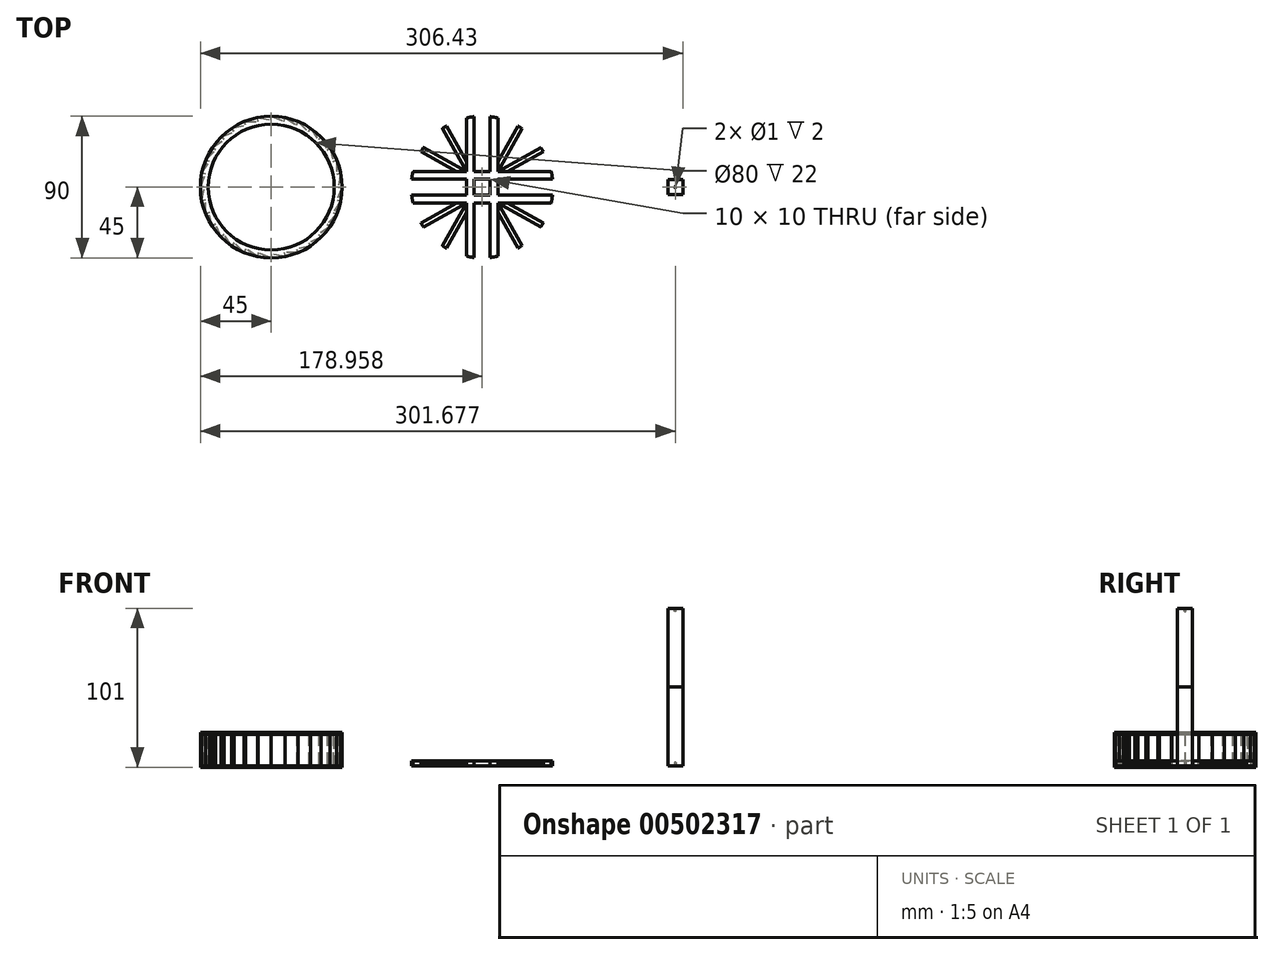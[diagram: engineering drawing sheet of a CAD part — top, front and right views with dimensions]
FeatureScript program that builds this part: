
annotation { "Feature Type Name" : "Feature", "Feature Type Description" : "" }
export const myFeature = defineFeature(function(context is Context, id is Id, definition is map)
    precondition{}
    {
        {
            var Q0;
            Q0=qCreatedBy(makeId("Top.planeOp"),FACE);
            var sketch = newSketch(context, id + "F0", { "sketchPlane" : qUnion([Q0])});
            skCircle(sketch, "E0", {"center": v(0, 0) * mm, "radius": 4.5 * mm});
            skCircle(sketch, "E1", {"center": v(0, 0) * mm, "radius": 4 * mm});
            skLineSegment(sketch, "E2", {"start": v(0, 0) * mm, "end": v(0, 4.5) * mm, "construction": true});
            skLineSegment(sketch, "E3.1.0", {"start": v(0, 0) * mm, "end": v(-0.88, 4.41) * mm, "construction": true});
            skLineSegment(sketch, "E3.2.0", {"start": v(0, 0) * mm, "end": v(-1.72, 4.16) * mm, "construction": true});
            skLineSegment(sketch, "E3.3.0", {"start": v(0, 0) * mm, "end": v(-2.5, 3.74) * mm, "construction": true});
            skLineSegment(sketch, "E3.4.0", {"start": v(0, 0) * mm, "end": v(-3.18, 3.18) * mm, "construction": true});
            skLineSegment(sketch, "E3.5.0", {"start": v(0, 0) * mm, "end": v(-3.74, 2.5) * mm, "construction": true});
            skLineSegment(sketch, "E3.6.0", {"start": v(0, 0) * mm, "end": v(-4.16, 1.72) * mm, "construction": true});
            skLineSegment(sketch, "E3.7.0", {"start": v(0, 0) * mm, "end": v(-4.41, 0.88) * mm, "construction": true});
            skLineSegment(sketch, "E3.8.0", {"start": v(0, 0) * mm, "end": v(-4.5, 0) * mm, "construction": true});
            skLineSegment(sketch, "E3.9.0", {"start": v(0, 0) * mm, "end": v(-4.41, -0.88) * mm, "construction": true});
            skLineSegment(sketch, "E3.10.0", {"start": v(0, 0) * mm, "end": v(-4.16, -1.72) * mm, "construction": true});
            skLineSegment(sketch, "E3.11.0", {"start": v(0, 0) * mm, "end": v(-3.74, -2.5) * mm, "construction": true});
            skLineSegment(sketch, "E3.12.0", {"start": v(0, 0) * mm, "end": v(-3.18, -3.18) * mm, "construction": true});
            skLineSegment(sketch, "E3.13.0", {"start": v(0, 0) * mm, "end": v(-2.5, -3.74) * mm, "construction": true});
            skLineSegment(sketch, "E3.14.0", {"start": v(0, 0) * mm, "end": v(-1.72, -4.16) * mm, "construction": true});
            skLineSegment(sketch, "E3.15.0", {"start": v(0, 0) * mm, "end": v(-0.88, -4.41) * mm, "construction": true});
            skLineSegment(sketch, "E3.16.0", {"start": v(0, 0) * mm, "end": v(0, -4.5) * mm, "construction": true});
            skLineSegment(sketch, "E3.17.0", {"start": v(0, 0) * mm, "end": v(0.88, -4.41) * mm, "construction": true});
            skLineSegment(sketch, "E3.18.0", {"start": v(0, 0) * mm, "end": v(1.72, -4.16) * mm, "construction": true});
            skLineSegment(sketch, "E3.19.0", {"start": v(0, 0) * mm, "end": v(2.5, -3.74) * mm, "construction": true});
            skLineSegment(sketch, "E3.20.0", {"start": v(0, 0) * mm, "end": v(3.18, -3.18) * mm, "construction": true});
            skLineSegment(sketch, "E3.21.0", {"start": v(0, 0) * mm, "end": v(3.74, -2.5) * mm, "construction": true});
            skLineSegment(sketch, "E3.22.0", {"start": v(0, 0) * mm, "end": v(4.16, -1.72) * mm, "construction": true});
            skLineSegment(sketch, "E3.23.0", {"start": v(0, 0) * mm, "end": v(4.41, -0.88) * mm, "construction": true});
            skLineSegment(sketch, "E3.24.0", {"start": v(0, 0) * mm, "end": v(4.5, 0) * mm, "construction": true});
            skLineSegment(sketch, "E3.25.0", {"start": v(0, 0) * mm, "end": v(4.41, 0.88) * mm, "construction": true});
            skLineSegment(sketch, "E3.26.0", {"start": v(0, 0) * mm, "end": v(4.16, 1.72) * mm, "construction": true});
            skLineSegment(sketch, "E3.27.0", {"start": v(0, 0) * mm, "end": v(3.74, 2.5) * mm, "construction": true});
            skLineSegment(sketch, "E3.28.0", {"start": v(0, 0) * mm, "end": v(3.18, 3.18) * mm, "construction": true});
            skLineSegment(sketch, "E3.29.0", {"start": v(0, 0) * mm, "end": v(2.5, 3.74) * mm, "construction": true});
            skLineSegment(sketch, "E3.30.0", {"start": v(0, 0) * mm, "end": v(1.72, 4.16) * mm, "construction": true});
            skLineSegment(sketch, "E3.31.0", {"start": v(0, 0) * mm, "end": v(0.88, 4.41) * mm, "construction": true});
            skCircle(sketch, "E4", {"center": v(0, 0) * mm, "radius": 4.25 * mm, "construction": true});
            skLineSegment(sketch, "E5", {"start": v(0, 4.25) * mm, "end": v(0, 4.5) * mm});
            skLineSegment(sketch, "E6", {"start": v(0, 4.5) * mm, "end": v(0.83, 4.17) * mm});
            skLineSegment(sketch, "E7.1.0", {"start": v(-0.88, 4.41) * mm, "end": v(0, 4.25) * mm});
            skLineSegment(sketch, "E7.1.1", {"start": v(-0.83, 4.17) * mm, "end": v(-0.88, 4.41) * mm});
            skLineSegment(sketch, "E7.2.0", {"start": v(-1.72, 4.16) * mm, "end": v(-0.83, 4.17) * mm});
            skLineSegment(sketch, "E7.2.1", {"start": v(-1.63, 3.93) * mm, "end": v(-1.72, 4.16) * mm});
            skLineSegment(sketch, "E7.3.0", {"start": v(-2.5, 3.74) * mm, "end": v(-1.63, 3.93) * mm});
            skLineSegment(sketch, "E7.3.1", {"start": v(-2.36, 3.53) * mm, "end": v(-2.5, 3.74) * mm});
            skLineSegment(sketch, "E7.4.0", {"start": v(-3.18, 3.18) * mm, "end": v(-2.36, 3.53) * mm});
            skLineSegment(sketch, "E7.4.1", {"start": v(-3, 3) * mm, "end": v(-3.18, 3.18) * mm});
            skLineSegment(sketch, "E7.5.0", {"start": v(-3.74, 2.5) * mm, "end": v(-3, 3) * mm});
            skLineSegment(sketch, "E7.5.1", {"start": v(-3.53, 2.36) * mm, "end": v(-3.74, 2.5) * mm});
            skLineSegment(sketch, "E7.6.0", {"start": v(-4.16, 1.72) * mm, "end": v(-3.53, 2.36) * mm});
            skLineSegment(sketch, "E7.6.1", {"start": v(-3.93, 1.63) * mm, "end": v(-4.16, 1.72) * mm});
            skLineSegment(sketch, "E7.7.0", {"start": v(-4.41, 0.88) * mm, "end": v(-3.93, 1.63) * mm});
            skLineSegment(sketch, "E7.7.1", {"start": v(-4.17, 0.83) * mm, "end": v(-4.41, 0.88) * mm});
            skLineSegment(sketch, "E7.8.0", {"start": v(-4.5, 0) * mm, "end": v(-4.17, 0.83) * mm});
            skLineSegment(sketch, "E7.8.1", {"start": v(-4.25, 0) * mm, "end": v(-4.5, 0) * mm});
            skLineSegment(sketch, "E7.9.0", {"start": v(-4.41, -0.88) * mm, "end": v(-4.25, 0) * mm});
            skLineSegment(sketch, "E7.9.1", {"start": v(-4.17, -0.83) * mm, "end": v(-4.41, -0.88) * mm});
            skLineSegment(sketch, "E7.10.0", {"start": v(-4.16, -1.72) * mm, "end": v(-4.17, -0.83) * mm});
            skLineSegment(sketch, "E7.10.1", {"start": v(-3.93, -1.63) * mm, "end": v(-4.16, -1.72) * mm});
            skLineSegment(sketch, "E7.11.0", {"start": v(-3.74, -2.5) * mm, "end": v(-3.93, -1.63) * mm});
            skLineSegment(sketch, "E7.11.1", {"start": v(-3.53, -2.36) * mm, "end": v(-3.74, -2.5) * mm});
            skLineSegment(sketch, "E7.12.0", {"start": v(-3.18, -3.18) * mm, "end": v(-3.53, -2.36) * mm});
            skLineSegment(sketch, "E7.12.1", {"start": v(-3, -3) * mm, "end": v(-3.18, -3.18) * mm});
            skLineSegment(sketch, "E7.13.0", {"start": v(-2.5, -3.74) * mm, "end": v(-3, -3) * mm});
            skLineSegment(sketch, "E7.13.1", {"start": v(-2.36, -3.53) * mm, "end": v(-2.5, -3.74) * mm});
            skLineSegment(sketch, "E7.14.0", {"start": v(-1.72, -4.16) * mm, "end": v(-2.36, -3.53) * mm});
            skLineSegment(sketch, "E7.14.1", {"start": v(-1.63, -3.93) * mm, "end": v(-1.72, -4.16) * mm});
            skLineSegment(sketch, "E7.15.0", {"start": v(-0.88, -4.41) * mm, "end": v(-1.63, -3.93) * mm});
            skLineSegment(sketch, "E7.15.1", {"start": v(-0.83, -4.17) * mm, "end": v(-0.88, -4.41) * mm});
            skLineSegment(sketch, "E7.16.0", {"start": v(0, -4.5) * mm, "end": v(-0.83, -4.17) * mm});
            skLineSegment(sketch, "E7.16.1", {"start": v(0, -4.25) * mm, "end": v(0, -4.5) * mm});
            skLineSegment(sketch, "E7.17.0", {"start": v(0.88, -4.41) * mm, "end": v(0, -4.25) * mm});
            skLineSegment(sketch, "E7.17.1", {"start": v(0.83, -4.17) * mm, "end": v(0.88, -4.41) * mm});
            skLineSegment(sketch, "E7.18.0", {"start": v(1.72, -4.16) * mm, "end": v(0.83, -4.17) * mm});
            skLineSegment(sketch, "E7.18.1", {"start": v(1.63, -3.93) * mm, "end": v(1.72, -4.16) * mm});
            skLineSegment(sketch, "E7.19.0", {"start": v(2.5, -3.74) * mm, "end": v(1.63, -3.93) * mm});
            skLineSegment(sketch, "E7.19.1", {"start": v(2.36, -3.53) * mm, "end": v(2.5, -3.74) * mm});
            skLineSegment(sketch, "E7.20.0", {"start": v(3.18, -3.18) * mm, "end": v(2.36, -3.53) * mm});
            skLineSegment(sketch, "E7.20.1", {"start": v(3, -3) * mm, "end": v(3.18, -3.18) * mm});
            skLineSegment(sketch, "E7.21.0", {"start": v(3.74, -2.5) * mm, "end": v(3, -3) * mm});
            skLineSegment(sketch, "E7.21.1", {"start": v(3.53, -2.36) * mm, "end": v(3.74, -2.5) * mm});
            skLineSegment(sketch, "E7.22.0", {"start": v(4.16, -1.72) * mm, "end": v(3.53, -2.36) * mm});
            skLineSegment(sketch, "E7.22.1", {"start": v(3.93, -1.63) * mm, "end": v(4.16, -1.72) * mm});
            skLineSegment(sketch, "E7.23.0", {"start": v(4.41, -0.88) * mm, "end": v(3.93, -1.63) * mm});
            skLineSegment(sketch, "E7.23.1", {"start": v(4.17, -0.83) * mm, "end": v(4.41, -0.88) * mm});
            skLineSegment(sketch, "E7.24.0", {"start": v(4.5, 0) * mm, "end": v(4.17, -0.83) * mm});
            skLineSegment(sketch, "E7.24.1", {"start": v(4.25, 0) * mm, "end": v(4.5, 0) * mm});
            skLineSegment(sketch, "E7.25.0", {"start": v(4.41, 0.88) * mm, "end": v(4.25, 0) * mm});
            skLineSegment(sketch, "E7.25.1", {"start": v(4.17, 0.83) * mm, "end": v(4.41, 0.88) * mm});
            skLineSegment(sketch, "E7.26.0", {"start": v(4.16, 1.72) * mm, "end": v(4.17, 0.83) * mm});
            skLineSegment(sketch, "E7.26.1", {"start": v(3.93, 1.63) * mm, "end": v(4.16, 1.72) * mm});
            skLineSegment(sketch, "E7.27.0", {"start": v(3.74, 2.5) * mm, "end": v(3.93, 1.63) * mm});
            skLineSegment(sketch, "E7.27.1", {"start": v(3.53, 2.36) * mm, "end": v(3.74, 2.5) * mm});
            skLineSegment(sketch, "E7.28.0", {"start": v(3.18, 3.18) * mm, "end": v(3.53, 2.36) * mm});
            skLineSegment(sketch, "E7.28.1", {"start": v(3, 3) * mm, "end": v(3.18, 3.18) * mm});
            skLineSegment(sketch, "E7.29.0", {"start": v(2.5, 3.74) * mm, "end": v(3, 3) * mm});
            skLineSegment(sketch, "E7.29.1", {"start": v(2.36, 3.53) * mm, "end": v(2.5, 3.74) * mm});
            skLineSegment(sketch, "E7.30.0", {"start": v(1.72, 4.16) * mm, "end": v(2.36, 3.53) * mm});
            skLineSegment(sketch, "E7.30.1", {"start": v(1.63, 3.93) * mm, "end": v(1.72, 4.16) * mm});
            skLineSegment(sketch, "E7.31.0", {"start": v(0.88, 4.41) * mm, "end": v(1.63, 3.93) * mm});
            skLineSegment(sketch, "E7.31.1", {"start": v(0.83, 4.17) * mm, "end": v(0.88, 4.41) * mm});
            skSolve(sketch);
        }
        {
            var Q0;
            Q0=makeQuery(id+"F0.imprint","IMPRINT",FACE,{"disambiguationData":[TD([[makeQuery(id+"F0.imprint","IMPRINT",EDGE,{"derivedFrom":sQuery(id+"F0.wireOp",EDGE,"E1")}),-1.0]])]});
            extrude(context, id + "F1", {"entities" : qUnion([Q0]), "depth" : 1 * mm});
        }
        {
            var Q0;
            {var subQ0=sQuery(id+"F0.wireOp",EDGE,"E7.29.1");Q0=makeQuery(id+"F0.imprint","IMPRINT",FACE,{"disambiguationData":[TD([[makeQuery(id+"F0.imprint","IMPRINT",EDGE,{"derivedFrom":subQ0}),1.0]])]});}
            var Q1;
            {var subQ0=sQuery(id+"F0.wireOp",EDGE,"E7.6.1");Q1=makeQuery(id+"F0.imprint","IMPRINT",FACE,{"disambiguationData":[TD([[makeQuery(id+"F0.imprint","IMPRINT",EDGE,{"derivedFrom":subQ0}),1.0]])]});}
            var Q2;
            {var subQ0=sQuery(id+"F0.wireOp",EDGE,"E7.18.1");Q2=makeQuery(id+"F0.imprint","IMPRINT",FACE,{"disambiguationData":[TD([[makeQuery(id+"F0.imprint","IMPRINT",EDGE,{"derivedFrom":subQ0}),1.0]])]});}
            var Q3;
            {var subQ0=sQuery(id+"F0.wireOp",EDGE,"E7.28.1");Q3=makeQuery(id+"F0.imprint","IMPRINT",FACE,{"disambiguationData":[TD([[makeQuery(id+"F0.imprint","IMPRINT",EDGE,{"derivedFrom":subQ0}),1.0]])]});}
            var Q4;
            {var subQ0=sQuery(id+"F0.wireOp",EDGE,"E7.8.1");Q4=makeQuery(id+"F0.imprint","IMPRINT",FACE,{"disambiguationData":[TD([[makeQuery(id+"F0.imprint","IMPRINT",EDGE,{"derivedFrom":subQ0}),1.0]])]});}
            var Q5;
            {var subQ0=sQuery(id+"F0.wireOp",EDGE,"E7.26.1");Q5=makeQuery(id+"F0.imprint","IMPRINT",FACE,{"disambiguationData":[TD([[makeQuery(id+"F0.imprint","IMPRINT",EDGE,{"derivedFrom":subQ0}),1.0]])]});}
            var Q6;
            {var subQ0=sQuery(id+"F0.wireOp",EDGE,"E7.7.1");Q6=makeQuery(id+"F0.imprint","IMPRINT",FACE,{"disambiguationData":[TD([[makeQuery(id+"F0.imprint","IMPRINT",EDGE,{"derivedFrom":subQ0}),1.0]])]});}
            var Q7;
            {var subQ0=sQuery(id+"F0.wireOp",EDGE,"E7.10.1");Q7=makeQuery(id+"F0.imprint","IMPRINT",FACE,{"disambiguationData":[TD([[makeQuery(id+"F0.imprint","IMPRINT",EDGE,{"derivedFrom":subQ0}),1.0]])]});}
            var Q8;
            {var subQ0=sQuery(id+"F0.wireOp",EDGE,"E7.24.1");Q8=makeQuery(id+"F0.imprint","IMPRINT",FACE,{"disambiguationData":[TD([[makeQuery(id+"F0.imprint","IMPRINT",EDGE,{"derivedFrom":subQ0}),1.0]])]});}
            var Q9;
            {var subQ0=sQuery(id+"F0.wireOp",EDGE,"E7.23.1");Q9=makeQuery(id+"F0.imprint","IMPRINT",FACE,{"disambiguationData":[TD([[makeQuery(id+"F0.imprint","IMPRINT",EDGE,{"derivedFrom":subQ0}),1.0]])]});}
            var Q10;
            {var subQ0=sQuery(id+"F0.wireOp",EDGE,"E7.4.1");Q10=makeQuery(id+"F0.imprint","IMPRINT",FACE,{"disambiguationData":[TD([[makeQuery(id+"F0.imprint","IMPRINT",EDGE,{"derivedFrom":subQ0}),1.0]])]});}
            var Q11;
            {var subQ0=sQuery(id+"F0.wireOp",EDGE,"E7.20.1");Q11=makeQuery(id+"F0.imprint","IMPRINT",FACE,{"disambiguationData":[TD([[makeQuery(id+"F0.imprint","IMPRINT",EDGE,{"derivedFrom":subQ0}),1.0]])]});}
            var Q12;
            {var subQ0=sQuery(id+"F0.wireOp",EDGE,"E7.3.1");Q12=makeQuery(id+"F0.imprint","IMPRINT",FACE,{"disambiguationData":[TD([[makeQuery(id+"F0.imprint","IMPRINT",EDGE,{"derivedFrom":subQ0}),1.0]])]});}
            var Q13;
            {var subQ0=sQuery(id+"F0.wireOp",EDGE,"E7.13.1");Q13=makeQuery(id+"F0.imprint","IMPRINT",FACE,{"disambiguationData":[TD([[makeQuery(id+"F0.imprint","IMPRINT",EDGE,{"derivedFrom":subQ0}),1.0]])]});}
            var Q14;
            {var subQ0=sQuery(id+"F0.wireOp",EDGE,"E7.14.1");Q14=makeQuery(id+"F0.imprint","IMPRINT",FACE,{"disambiguationData":[TD([[makeQuery(id+"F0.imprint","IMPRINT",EDGE,{"derivedFrom":subQ0}),1.0]])]});}
            var Q15;
            {var subQ0=sQuery(id+"F0.wireOp",EDGE,"E7.17.1");Q15=makeQuery(id+"F0.imprint","IMPRINT",FACE,{"disambiguationData":[TD([[makeQuery(id+"F0.imprint","IMPRINT",EDGE,{"derivedFrom":subQ0}),1.0]])]});}
            var Q16;
            {var subQ0=sQuery(id+"F0.wireOp",EDGE,"E7.11.1");Q16=makeQuery(id+"F0.imprint","IMPRINT",FACE,{"disambiguationData":[TD([[makeQuery(id+"F0.imprint","IMPRINT",EDGE,{"derivedFrom":subQ0}),1.0]])]});}
            var Q17;
            {var subQ0=sQuery(id+"F0.wireOp",EDGE,"E7.19.1");Q17=makeQuery(id+"F0.imprint","IMPRINT",FACE,{"disambiguationData":[TD([[makeQuery(id+"F0.imprint","IMPRINT",EDGE,{"derivedFrom":subQ0}),1.0]])]});}
            var Q18;
            {var subQ0=sQuery(id+"F0.wireOp",EDGE,"E7.1.1");Q18=makeQuery(id+"F0.imprint","IMPRINT",FACE,{"disambiguationData":[TD([[makeQuery(id+"F0.imprint","IMPRINT",EDGE,{"derivedFrom":subQ0}),1.0]])]});}
            var Q19;
            Q19=makeQuery(id+"F0.imprint","IMPRINT",FACE,{"disambiguationData":[TD([[makeQuery(id+"F0.imprint","IMPRINT",EDGE,{"derivedFrom":sQuery(id+"F0.wireOp",EDGE,"E1")}),-1.0]])]});
            var Q20;
            {var subQ0=sQuery(id+"F0.wireOp",EDGE,"E7.5.1");Q20=makeQuery(id+"F0.imprint","IMPRINT",FACE,{"disambiguationData":[TD([[makeQuery(id+"F0.imprint","IMPRINT",EDGE,{"derivedFrom":subQ0}),1.0]])]});}
            var Q21;
            {var subQ0=sQuery(id+"F0.wireOp",EDGE,"E7.16.1");Q21=makeQuery(id+"F0.imprint","IMPRINT",FACE,{"disambiguationData":[TD([[makeQuery(id+"F0.imprint","IMPRINT",EDGE,{"derivedFrom":subQ0}),1.0]])]});}
            var Q22;
            {var subQ0=sQuery(id+"F0.wireOp",EDGE,"E7.25.1");Q22=makeQuery(id+"F0.imprint","IMPRINT",FACE,{"disambiguationData":[TD([[makeQuery(id+"F0.imprint","IMPRINT",EDGE,{"derivedFrom":subQ0}),1.0]])]});}
            var Q23;
            {var subQ0=sQuery(id+"F0.wireOp",EDGE,"E7.12.1");Q23=makeQuery(id+"F0.imprint","IMPRINT",FACE,{"disambiguationData":[TD([[makeQuery(id+"F0.imprint","IMPRINT",EDGE,{"derivedFrom":subQ0}),1.0]])]});}
            var Q24;
            {var subQ0=sQuery(id+"F0.wireOp",EDGE,"E7.2.1");Q24=makeQuery(id+"F0.imprint","IMPRINT",FACE,{"disambiguationData":[TD([[makeQuery(id+"F0.imprint","IMPRINT",EDGE,{"derivedFrom":subQ0}),1.0]])]});}
            var Q25;
            {var subQ0=sQuery(id+"F0.wireOp",EDGE,"E7.9.1");Q25=makeQuery(id+"F0.imprint","IMPRINT",FACE,{"disambiguationData":[TD([[makeQuery(id+"F0.imprint","IMPRINT",EDGE,{"derivedFrom":subQ0}),1.0]])]});}
            var Q26;
            {var subQ0=sQuery(id+"F0.wireOp",EDGE,"E7.30.1");Q26=makeQuery(id+"F0.imprint","IMPRINT",FACE,{"disambiguationData":[TD([[makeQuery(id+"F0.imprint","IMPRINT",EDGE,{"derivedFrom":subQ0}),1.0]])]});}
            var Q27;
            {var subQ0=sQuery(id+"F0.wireOp",EDGE,"E7.27.1");Q27=makeQuery(id+"F0.imprint","IMPRINT",FACE,{"disambiguationData":[TD([[makeQuery(id+"F0.imprint","IMPRINT",EDGE,{"derivedFrom":subQ0}),1.0]])]});}
            var Q28;
            {var subQ0=sQuery(id+"F0.wireOp",EDGE,"E5");Q28=makeQuery(id+"F0.imprint","IMPRINT",FACE,{"disambiguationData":[TD([[makeQuery(id+"F0.imprint","IMPRINT",EDGE,{"derivedFrom":subQ0}),1.0]])]});}
            var Q29;
            {var subQ0=sQuery(id+"F0.wireOp",EDGE,"E7.21.1");Q29=makeQuery(id+"F0.imprint","IMPRINT",FACE,{"disambiguationData":[TD([[makeQuery(id+"F0.imprint","IMPRINT",EDGE,{"derivedFrom":subQ0}),1.0]])]});}
            var Q30;
            {var subQ0=sQuery(id+"F0.wireOp",EDGE,"E7.22.1");Q30=makeQuery(id+"F0.imprint","IMPRINT",FACE,{"disambiguationData":[TD([[makeQuery(id+"F0.imprint","IMPRINT",EDGE,{"derivedFrom":subQ0}),1.0]])]});}
            var Q31;
            {var subQ0=sQuery(id+"F0.wireOp",EDGE,"E6");Q31=makeQuery(id+"F0.imprint","IMPRINT",FACE,{"disambiguationData":[TD([[makeQuery(id+"F0.imprint","IMPRINT",EDGE,{"derivedFrom":subQ0}),1.0]])]});}
            var Q32;
            {var subQ0=sQuery(id+"F0.wireOp",EDGE,"E7.15.1");Q32=makeQuery(id+"F0.imprint","IMPRINT",FACE,{"disambiguationData":[TD([[makeQuery(id+"F0.imprint","IMPRINT",EDGE,{"derivedFrom":subQ0}),1.0]])]});}
            extrude(context, id + "F2", {"entities" : qUnion([Q0, Q1, Q2, Q3, Q4, Q5, Q6, Q7, Q8, Q9, Q10, Q11, Q12, Q13, Q14, Q15, Q16, Q17, Q18, Q19, Q20, Q21, Q22, Q23, Q24, Q25, Q26, Q27, Q28, Q29, Q30, Q31, Q32]), "oppositeDirection" : true, "depth" : .1 * mm});
        }
        {
            var Q0;
            Q0=makeQuery(id+"F2.opExtrude","SWEPT_BODY",BODY,{"disambiguationData":[OSD([sQuery(id+"F0.wireOp",EDGE,"E0"),sQuery(id+"F0.wireOp",EDGE,"E1")])]});
            var Q1;
            Q1=makeQuery(id+"F1.opExtrude","SWEPT_BODY",BODY,{"disambiguationData":[OSD([sQuery(id+"F0.wireOp",EDGE,"fD5KU7R1-ByY7-Rftd-DOh4-sofIxbQwviTQ"),sQuery(id+"F0.wireOp",EDGE,"ZJwh980X-72V5-jxd2-dHy7-HPEGcyYmpB0N"),sQuery(id+"F0.wireOp",EDGE,"fbb3889d-43d2-4d93-b0f5-646fe2721000.1.0"),sQuery(id+"F0.wireOp",EDGE,"fbb3889d-43d2-4d93-b0f5-646fe2721000.1.1"),sQuery(id+"F0.wireOp",EDGE,"fbb3889d-43d2-4d93-b0f5-646fe2721000.2.0"),sQuery(id+"F0.wireOp",EDGE,"fbb3889d-43d2-4d93-b0f5-646fe2721000.2.1"),sQuery(id+"F0.wireOp",EDGE,"fbb3889d-43d2-4d93-b0f5-646fe2721000.3.0"),sQuery(id+"F0.wireOp",EDGE,"fbb3889d-43d2-4d93-b0f5-646fe2721000.3.1"),sQuery(id+"F0.wireOp",EDGE,"fbb3889d-43d2-4d93-b0f5-646fe2721000.4.0"),sQuery(id+"F0.wireOp",EDGE,"fbb3889d-43d2-4d93-b0f5-646fe2721000.4.1"),sQuery(id+"F0.wireOp",EDGE,"fbb3889d-43d2-4d93-b0f5-646fe2721000.5.0"),sQuery(id+"F0.wireOp",EDGE,"fbb3889d-43d2-4d93-b0f5-646fe2721000.5.1"),sQuery(id+"F0.wireOp",EDGE,"fbb3889d-43d2-4d93-b0f5-646fe2721000.6.0"),sQuery(id+"F0.wireOp",EDGE,"fbb3889d-43d2-4d93-b0f5-646fe2721000.6.1"),sQuery(id+"F0.wireOp",EDGE,"fbb3889d-43d2-4d93-b0f5-646fe2721000.7.0"),sQuery(id+"F0.wireOp",EDGE,"fbb3889d-43d2-4d93-b0f5-646fe2721000.7.1"),sQuery(id+"F0.wireOp",EDGE,"fbb3889d-43d2-4d93-b0f5-646fe2721000.8.0"),sQuery(id+"F0.wireOp",EDGE,"fbb3889d-43d2-4d93-b0f5-646fe2721000.8.1"),sQuery(id+"F0.wireOp",EDGE,"fbb3889d-43d2-4d93-b0f5-646fe2721000.9.0"),sQuery(id+"F0.wireOp",EDGE,"fbb3889d-43d2-4d93-b0f5-646fe2721000.9.1"),sQuery(id+"F0.wireOp",EDGE,"fbb3889d-43d2-4d93-b0f5-646fe2721000.10.0"),sQuery(id+"F0.wireOp",EDGE,"fbb3889d-43d2-4d93-b0f5-646fe2721000.10.1"),sQuery(id+"F0.wireOp",EDGE,"fbb3889d-43d2-4d93-b0f5-646fe2721000.11.0"),sQuery(id+"F0.wireOp",EDGE,"fbb3889d-43d2-4d93-b0f5-646fe2721000.11.1"),sQuery(id+"F0.wireOp",EDGE,"fbb3889d-43d2-4d93-b0f5-646fe2721000.12.0"),sQuery(id+"F0.wireOp",EDGE,"fbb3889d-43d2-4d93-b0f5-646fe2721000.12.1"),sQuery(id+"F0.wireOp",EDGE,"fbb3889d-43d2-4d93-b0f5-646fe2721000.13.0"),sQuery(id+"F0.wireOp",EDGE,"fbb3889d-43d2-4d93-b0f5-646fe2721000.13.1"),sQuery(id+"F0.wireOp",EDGE,"fbb3889d-43d2-4d93-b0f5-646fe2721000.14.0"),sQuery(id+"F0.wireOp",EDGE,"fbb3889d-43d2-4d93-b0f5-646fe2721000.14.1"),sQuery(id+"F0.wireOp",EDGE,"fbb3889d-43d2-4d93-b0f5-646fe2721000.15.0"),sQuery(id+"F0.wireOp",EDGE,"fbb3889d-43d2-4d93-b0f5-646fe2721000.15.1"),sQuery(id+"F0.wireOp",EDGE,"fbb3889d-43d2-4d93-b0f5-646fe2721000.16.0"),sQuery(id+"F0.wireOp",EDGE,"fbb3889d-43d2-4d93-b0f5-646fe2721000.16.1"),sQuery(id+"F0.wireOp",EDGE,"fbb3889d-43d2-4d93-b0f5-646fe2721000.17.0"),sQuery(id+"F0.wireOp",EDGE,"fbb3889d-43d2-4d93-b0f5-646fe2721000.17.1"),sQuery(id+"F0.wireOp",EDGE,"fbb3889d-43d2-4d93-b0f5-646fe2721000.18.0"),sQuery(id+"F0.wireOp",EDGE,"fbb3889d-43d2-4d93-b0f5-646fe2721000.18.1"),sQuery(id+"F0.wireOp",EDGE,"fbb3889d-43d2-4d93-b0f5-646fe2721000.19.0"),sQuery(id+"F0.wireOp",EDGE,"fbb3889d-43d2-4d93-b0f5-646fe2721000.19.1"),sQuery(id+"F0.wireOp",EDGE,"fbb3889d-43d2-4d93-b0f5-646fe2721000.20.0"),sQuery(id+"F0.wireOp",EDGE,"fbb3889d-43d2-4d93-b0f5-646fe2721000.20.1"),sQuery(id+"F0.wireOp",EDGE,"fbb3889d-43d2-4d93-b0f5-646fe2721000.21.0"),sQuery(id+"F0.wireOp",EDGE,"fbb3889d-43d2-4d93-b0f5-646fe2721000.21.1"),sQuery(id+"F0.wireOp",EDGE,"fbb3889d-43d2-4d93-b0f5-646fe2721000.22.0"),sQuery(id+"F0.wireOp",EDGE,"fbb3889d-43d2-4d93-b0f5-646fe2721000.22.1"),sQuery(id+"F0.wireOp",EDGE,"fbb3889d-43d2-4d93-b0f5-646fe2721000.23.0"),sQuery(id+"F0.wireOp",EDGE,"fbb3889d-43d2-4d93-b0f5-646fe2721000.23.1"),sQuery(id+"F0.wireOp",EDGE,"fbb3889d-43d2-4d93-b0f5-646fe2721000.24.0"),sQuery(id+"F0.wireOp",EDGE,"fbb3889d-43d2-4d93-b0f5-646fe2721000.24.1"),sQuery(id+"F0.wireOp",EDGE,"fbb3889d-43d2-4d93-b0f5-646fe2721000.25.0"),sQuery(id+"F0.wireOp",EDGE,"fbb3889d-43d2-4d93-b0f5-646fe2721000.25.1"),sQuery(id+"F0.wireOp",EDGE,"fbb3889d-43d2-4d93-b0f5-646fe2721000.26.0"),sQuery(id+"F0.wireOp",EDGE,"fbb3889d-43d2-4d93-b0f5-646fe2721000.26.1"),sQuery(id+"F0.wireOp",EDGE,"fbb3889d-43d2-4d93-b0f5-646fe2721000.27.0"),sQuery(id+"F0.wireOp",EDGE,"fbb3889d-43d2-4d93-b0f5-646fe2721000.27.1"),sQuery(id+"F0.wireOp",EDGE,"fbb3889d-43d2-4d93-b0f5-646fe2721000.28.0"),sQuery(id+"F0.wireOp",EDGE,"fbb3889d-43d2-4d93-b0f5-646fe2721000.28.1"),sQuery(id+"F0.wireOp",EDGE,"fbb3889d-43d2-4d93-b0f5-646fe2721000.29.0"),sQuery(id+"F0.wireOp",EDGE,"fbb3889d-43d2-4d93-b0f5-646fe2721000.29.1"),sQuery(id+"F0.wireOp",EDGE,"fbb3889d-43d2-4d93-b0f5-646fe2721000.30.0"),sQuery(id+"F0.wireOp",EDGE,"fbb3889d-43d2-4d93-b0f5-646fe2721000.30.1"),sQuery(id+"F0.wireOp",EDGE,"fbb3889d-43d2-4d93-b0f5-646fe2721000.31.0"),sQuery(id+"F0.wireOp",EDGE,"fbb3889d-43d2-4d93-b0f5-646fe2721000.31.1"),sQuery(id+"F0.wireOp",EDGE,"E1")])]});
            var Q2;
            Q2=makeQuery(id+"F1.opExtrude","CAP_FACE",FACE,{"disambiguationData":[OSD([sQuery(id+"F0.wireOp",EDGE,"fD5KU7R1-ByY7-Rftd-DOh4-sofIxbQwviTQ"),sQuery(id+"F0.wireOp",EDGE,"ZJwh980X-72V5-jxd2-dHy7-HPEGcyYmpB0N"),sQuery(id+"F0.wireOp",EDGE,"fbb3889d-43d2-4d93-b0f5-646fe2721000.1.0"),sQuery(id+"F0.wireOp",EDGE,"fbb3889d-43d2-4d93-b0f5-646fe2721000.1.1"),sQuery(id+"F0.wireOp",EDGE,"fbb3889d-43d2-4d93-b0f5-646fe2721000.2.0"),sQuery(id+"F0.wireOp",EDGE,"fbb3889d-43d2-4d93-b0f5-646fe2721000.2.1"),sQuery(id+"F0.wireOp",EDGE,"fbb3889d-43d2-4d93-b0f5-646fe2721000.3.0"),sQuery(id+"F0.wireOp",EDGE,"fbb3889d-43d2-4d93-b0f5-646fe2721000.3.1"),sQuery(id+"F0.wireOp",EDGE,"fbb3889d-43d2-4d93-b0f5-646fe2721000.4.0"),sQuery(id+"F0.wireOp",EDGE,"fbb3889d-43d2-4d93-b0f5-646fe2721000.4.1"),sQuery(id+"F0.wireOp",EDGE,"fbb3889d-43d2-4d93-b0f5-646fe2721000.5.0"),sQuery(id+"F0.wireOp",EDGE,"fbb3889d-43d2-4d93-b0f5-646fe2721000.5.1"),sQuery(id+"F0.wireOp",EDGE,"fbb3889d-43d2-4d93-b0f5-646fe2721000.6.0"),sQuery(id+"F0.wireOp",EDGE,"fbb3889d-43d2-4d93-b0f5-646fe2721000.6.1"),sQuery(id+"F0.wireOp",EDGE,"fbb3889d-43d2-4d93-b0f5-646fe2721000.7.0"),sQuery(id+"F0.wireOp",EDGE,"fbb3889d-43d2-4d93-b0f5-646fe2721000.7.1"),sQuery(id+"F0.wireOp",EDGE,"fbb3889d-43d2-4d93-b0f5-646fe2721000.8.0"),sQuery(id+"F0.wireOp",EDGE,"fbb3889d-43d2-4d93-b0f5-646fe2721000.8.1"),sQuery(id+"F0.wireOp",EDGE,"fbb3889d-43d2-4d93-b0f5-646fe2721000.9.0"),sQuery(id+"F0.wireOp",EDGE,"fbb3889d-43d2-4d93-b0f5-646fe2721000.9.1"),sQuery(id+"F0.wireOp",EDGE,"fbb3889d-43d2-4d93-b0f5-646fe2721000.10.0"),sQuery(id+"F0.wireOp",EDGE,"fbb3889d-43d2-4d93-b0f5-646fe2721000.10.1"),sQuery(id+"F0.wireOp",EDGE,"fbb3889d-43d2-4d93-b0f5-646fe2721000.11.0"),sQuery(id+"F0.wireOp",EDGE,"fbb3889d-43d2-4d93-b0f5-646fe2721000.11.1"),sQuery(id+"F0.wireOp",EDGE,"fbb3889d-43d2-4d93-b0f5-646fe2721000.12.0"),sQuery(id+"F0.wireOp",EDGE,"fbb3889d-43d2-4d93-b0f5-646fe2721000.12.1"),sQuery(id+"F0.wireOp",EDGE,"fbb3889d-43d2-4d93-b0f5-646fe2721000.13.0"),sQuery(id+"F0.wireOp",EDGE,"fbb3889d-43d2-4d93-b0f5-646fe2721000.13.1"),sQuery(id+"F0.wireOp",EDGE,"fbb3889d-43d2-4d93-b0f5-646fe2721000.14.0"),sQuery(id+"F0.wireOp",EDGE,"fbb3889d-43d2-4d93-b0f5-646fe2721000.14.1"),sQuery(id+"F0.wireOp",EDGE,"fbb3889d-43d2-4d93-b0f5-646fe2721000.15.0"),sQuery(id+"F0.wireOp",EDGE,"fbb3889d-43d2-4d93-b0f5-646fe2721000.15.1"),sQuery(id+"F0.wireOp",EDGE,"fbb3889d-43d2-4d93-b0f5-646fe2721000.16.0"),sQuery(id+"F0.wireOp",EDGE,"fbb3889d-43d2-4d93-b0f5-646fe2721000.16.1"),sQuery(id+"F0.wireOp",EDGE,"fbb3889d-43d2-4d93-b0f5-646fe2721000.17.0"),sQuery(id+"F0.wireOp",EDGE,"fbb3889d-43d2-4d93-b0f5-646fe2721000.17.1"),sQuery(id+"F0.wireOp",EDGE,"fbb3889d-43d2-4d93-b0f5-646fe2721000.18.0"),sQuery(id+"F0.wireOp",EDGE,"fbb3889d-43d2-4d93-b0f5-646fe2721000.18.1"),sQuery(id+"F0.wireOp",EDGE,"fbb3889d-43d2-4d93-b0f5-646fe2721000.19.0"),sQuery(id+"F0.wireOp",EDGE,"fbb3889d-43d2-4d93-b0f5-646fe2721000.19.1"),sQuery(id+"F0.wireOp",EDGE,"fbb3889d-43d2-4d93-b0f5-646fe2721000.20.0"),sQuery(id+"F0.wireOp",EDGE,"fbb3889d-43d2-4d93-b0f5-646fe2721000.20.1"),sQuery(id+"F0.wireOp",EDGE,"fbb3889d-43d2-4d93-b0f5-646fe2721000.21.0"),sQuery(id+"F0.wireOp",EDGE,"fbb3889d-43d2-4d93-b0f5-646fe2721000.21.1"),sQuery(id+"F0.wireOp",EDGE,"fbb3889d-43d2-4d93-b0f5-646fe2721000.22.0"),sQuery(id+"F0.wireOp",EDGE,"fbb3889d-43d2-4d93-b0f5-646fe2721000.22.1"),sQuery(id+"F0.wireOp",EDGE,"fbb3889d-43d2-4d93-b0f5-646fe2721000.23.0"),sQuery(id+"F0.wireOp",EDGE,"fbb3889d-43d2-4d93-b0f5-646fe2721000.23.1"),sQuery(id+"F0.wireOp",EDGE,"fbb3889d-43d2-4d93-b0f5-646fe2721000.24.0"),sQuery(id+"F0.wireOp",EDGE,"fbb3889d-43d2-4d93-b0f5-646fe2721000.24.1"),sQuery(id+"F0.wireOp",EDGE,"fbb3889d-43d2-4d93-b0f5-646fe2721000.25.0"),sQuery(id+"F0.wireOp",EDGE,"fbb3889d-43d2-4d93-b0f5-646fe2721000.25.1"),sQuery(id+"F0.wireOp",EDGE,"fbb3889d-43d2-4d93-b0f5-646fe2721000.26.0"),sQuery(id+"F0.wireOp",EDGE,"fbb3889d-43d2-4d93-b0f5-646fe2721000.26.1"),sQuery(id+"F0.wireOp",EDGE,"fbb3889d-43d2-4d93-b0f5-646fe2721000.27.0"),sQuery(id+"F0.wireOp",EDGE,"fbb3889d-43d2-4d93-b0f5-646fe2721000.27.1"),sQuery(id+"F0.wireOp",EDGE,"fbb3889d-43d2-4d93-b0f5-646fe2721000.28.0"),sQuery(id+"F0.wireOp",EDGE,"fbb3889d-43d2-4d93-b0f5-646fe2721000.28.1"),sQuery(id+"F0.wireOp",EDGE,"fbb3889d-43d2-4d93-b0f5-646fe2721000.29.0"),sQuery(id+"F0.wireOp",EDGE,"fbb3889d-43d2-4d93-b0f5-646fe2721000.29.1"),sQuery(id+"F0.wireOp",EDGE,"fbb3889d-43d2-4d93-b0f5-646fe2721000.30.0"),sQuery(id+"F0.wireOp",EDGE,"fbb3889d-43d2-4d93-b0f5-646fe2721000.30.1"),sQuery(id+"F0.wireOp",EDGE,"fbb3889d-43d2-4d93-b0f5-646fe2721000.31.0"),sQuery(id+"F0.wireOp",EDGE,"fbb3889d-43d2-4d93-b0f5-646fe2721000.31.1"),sQuery(id+"F0.wireOp",EDGE,"E1")])],"isStart":false});
            mirror(context, id + "F3", {"operationType" : NewBodyOperationType.ADD, "entities" : qUnion([Q0, Q1]), "mirrorPlane" : qUnion([Q2])});
        }
        {
            var Q0;
            Q0=makeQuery(id+"F1.opExtrude","SWEPT_BODY",BODY,{"disambiguationData":[OSD([sQuery(id+"F0.wireOp",EDGE,"fD5KU7R1-ByY7-Rftd-DOh4-sofIxbQwviTQ"),sQuery(id+"F0.wireOp",EDGE,"ZJwh980X-72V5-jxd2-dHy7-HPEGcyYmpB0N"),sQuery(id+"F0.wireOp",EDGE,"fbb3889d-43d2-4d93-b0f5-646fe2721000.1.0"),sQuery(id+"F0.wireOp",EDGE,"fbb3889d-43d2-4d93-b0f5-646fe2721000.1.1"),sQuery(id+"F0.wireOp",EDGE,"fbb3889d-43d2-4d93-b0f5-646fe2721000.2.0"),sQuery(id+"F0.wireOp",EDGE,"fbb3889d-43d2-4d93-b0f5-646fe2721000.2.1"),sQuery(id+"F0.wireOp",EDGE,"fbb3889d-43d2-4d93-b0f5-646fe2721000.3.0"),sQuery(id+"F0.wireOp",EDGE,"fbb3889d-43d2-4d93-b0f5-646fe2721000.3.1"),sQuery(id+"F0.wireOp",EDGE,"fbb3889d-43d2-4d93-b0f5-646fe2721000.4.0"),sQuery(id+"F0.wireOp",EDGE,"fbb3889d-43d2-4d93-b0f5-646fe2721000.4.1"),sQuery(id+"F0.wireOp",EDGE,"fbb3889d-43d2-4d93-b0f5-646fe2721000.5.0"),sQuery(id+"F0.wireOp",EDGE,"fbb3889d-43d2-4d93-b0f5-646fe2721000.5.1"),sQuery(id+"F0.wireOp",EDGE,"fbb3889d-43d2-4d93-b0f5-646fe2721000.6.0"),sQuery(id+"F0.wireOp",EDGE,"fbb3889d-43d2-4d93-b0f5-646fe2721000.6.1"),sQuery(id+"F0.wireOp",EDGE,"fbb3889d-43d2-4d93-b0f5-646fe2721000.7.0"),sQuery(id+"F0.wireOp",EDGE,"fbb3889d-43d2-4d93-b0f5-646fe2721000.7.1"),sQuery(id+"F0.wireOp",EDGE,"fbb3889d-43d2-4d93-b0f5-646fe2721000.8.0"),sQuery(id+"F0.wireOp",EDGE,"fbb3889d-43d2-4d93-b0f5-646fe2721000.8.1"),sQuery(id+"F0.wireOp",EDGE,"fbb3889d-43d2-4d93-b0f5-646fe2721000.9.0"),sQuery(id+"F0.wireOp",EDGE,"fbb3889d-43d2-4d93-b0f5-646fe2721000.9.1"),sQuery(id+"F0.wireOp",EDGE,"fbb3889d-43d2-4d93-b0f5-646fe2721000.10.0"),sQuery(id+"F0.wireOp",EDGE,"fbb3889d-43d2-4d93-b0f5-646fe2721000.10.1"),sQuery(id+"F0.wireOp",EDGE,"fbb3889d-43d2-4d93-b0f5-646fe2721000.11.0"),sQuery(id+"F0.wireOp",EDGE,"fbb3889d-43d2-4d93-b0f5-646fe2721000.11.1"),sQuery(id+"F0.wireOp",EDGE,"fbb3889d-43d2-4d93-b0f5-646fe2721000.12.0"),sQuery(id+"F0.wireOp",EDGE,"fbb3889d-43d2-4d93-b0f5-646fe2721000.12.1"),sQuery(id+"F0.wireOp",EDGE,"fbb3889d-43d2-4d93-b0f5-646fe2721000.13.0"),sQuery(id+"F0.wireOp",EDGE,"fbb3889d-43d2-4d93-b0f5-646fe2721000.13.1"),sQuery(id+"F0.wireOp",EDGE,"fbb3889d-43d2-4d93-b0f5-646fe2721000.14.0"),sQuery(id+"F0.wireOp",EDGE,"fbb3889d-43d2-4d93-b0f5-646fe2721000.14.1"),sQuery(id+"F0.wireOp",EDGE,"fbb3889d-43d2-4d93-b0f5-646fe2721000.15.0"),sQuery(id+"F0.wireOp",EDGE,"fbb3889d-43d2-4d93-b0f5-646fe2721000.15.1"),sQuery(id+"F0.wireOp",EDGE,"fbb3889d-43d2-4d93-b0f5-646fe2721000.16.0"),sQuery(id+"F0.wireOp",EDGE,"fbb3889d-43d2-4d93-b0f5-646fe2721000.16.1"),sQuery(id+"F0.wireOp",EDGE,"fbb3889d-43d2-4d93-b0f5-646fe2721000.17.0"),sQuery(id+"F0.wireOp",EDGE,"fbb3889d-43d2-4d93-b0f5-646fe2721000.17.1"),sQuery(id+"F0.wireOp",EDGE,"fbb3889d-43d2-4d93-b0f5-646fe2721000.18.0"),sQuery(id+"F0.wireOp",EDGE,"fbb3889d-43d2-4d93-b0f5-646fe2721000.18.1"),sQuery(id+"F0.wireOp",EDGE,"fbb3889d-43d2-4d93-b0f5-646fe2721000.19.0"),sQuery(id+"F0.wireOp",EDGE,"fbb3889d-43d2-4d93-b0f5-646fe2721000.19.1"),sQuery(id+"F0.wireOp",EDGE,"fbb3889d-43d2-4d93-b0f5-646fe2721000.20.0"),sQuery(id+"F0.wireOp",EDGE,"fbb3889d-43d2-4d93-b0f5-646fe2721000.20.1"),sQuery(id+"F0.wireOp",EDGE,"fbb3889d-43d2-4d93-b0f5-646fe2721000.21.0"),sQuery(id+"F0.wireOp",EDGE,"fbb3889d-43d2-4d93-b0f5-646fe2721000.21.1"),sQuery(id+"F0.wireOp",EDGE,"fbb3889d-43d2-4d93-b0f5-646fe2721000.22.0"),sQuery(id+"F0.wireOp",EDGE,"fbb3889d-43d2-4d93-b0f5-646fe2721000.22.1"),sQuery(id+"F0.wireOp",EDGE,"fbb3889d-43d2-4d93-b0f5-646fe2721000.23.0"),sQuery(id+"F0.wireOp",EDGE,"fbb3889d-43d2-4d93-b0f5-646fe2721000.23.1"),sQuery(id+"F0.wireOp",EDGE,"fbb3889d-43d2-4d93-b0f5-646fe2721000.24.0"),sQuery(id+"F0.wireOp",EDGE,"fbb3889d-43d2-4d93-b0f5-646fe2721000.24.1"),sQuery(id+"F0.wireOp",EDGE,"fbb3889d-43d2-4d93-b0f5-646fe2721000.25.0"),sQuery(id+"F0.wireOp",EDGE,"fbb3889d-43d2-4d93-b0f5-646fe2721000.25.1"),sQuery(id+"F0.wireOp",EDGE,"fbb3889d-43d2-4d93-b0f5-646fe2721000.26.0"),sQuery(id+"F0.wireOp",EDGE,"fbb3889d-43d2-4d93-b0f5-646fe2721000.26.1"),sQuery(id+"F0.wireOp",EDGE,"fbb3889d-43d2-4d93-b0f5-646fe2721000.27.0"),sQuery(id+"F0.wireOp",EDGE,"fbb3889d-43d2-4d93-b0f5-646fe2721000.27.1"),sQuery(id+"F0.wireOp",EDGE,"fbb3889d-43d2-4d93-b0f5-646fe2721000.28.0"),sQuery(id+"F0.wireOp",EDGE,"fbb3889d-43d2-4d93-b0f5-646fe2721000.28.1"),sQuery(id+"F0.wireOp",EDGE,"fbb3889d-43d2-4d93-b0f5-646fe2721000.29.0"),sQuery(id+"F0.wireOp",EDGE,"fbb3889d-43d2-4d93-b0f5-646fe2721000.29.1"),sQuery(id+"F0.wireOp",EDGE,"fbb3889d-43d2-4d93-b0f5-646fe2721000.30.0"),sQuery(id+"F0.wireOp",EDGE,"fbb3889d-43d2-4d93-b0f5-646fe2721000.30.1"),sQuery(id+"F0.wireOp",EDGE,"fbb3889d-43d2-4d93-b0f5-646fe2721000.31.0"),sQuery(id+"F0.wireOp",EDGE,"fbb3889d-43d2-4d93-b0f5-646fe2721000.31.1"),sQuery(id+"F0.wireOp",EDGE,"E1")])]});
            var Q1;
            Q1=makeQuery(id+"F2.opExtrude","SWEPT_BODY",BODY,{"disambiguationData":[OSD([sQuery(id+"F0.wireOp",EDGE,"E0"),sQuery(id+"F0.wireOp",EDGE,"E1")])]});
            var Q2;
            Q2=qCreatedBy(makeId("Origin.pointOp"),VERTEX);
            transform(context, id + "F4", {"entities" : qUnion([Q0, Q1]), "transformType" : TransformType.SCALE_UNIFORMLY, "scale" : 10, "scalePoint" : qUnion([Q2]), "makeCopy" : false});
        }
        {
            var Q0;
            Q0=qCreatedBy(makeId("Top.planeOp"),FACE);
            var sketch = newSketch(context, id + "F5", { "sketchPlane" : qUnion([Q0])});
            skCircle(sketch, "E8", {"center": v(133.96, 0) * mm, "radius": 45 * mm});
            skLineSegment(sketch, "E9", {"start": v(138.96, 0) * mm, "end": v(138.96, 5) * mm});
            skLineSegment(sketch, "E10.0", {"start": v(143.96, 0) * mm, "end": v(143.96, 5) * mm});
            skLineSegment(sketch, "E11", {"start": v(133.96, 45) * mm, "end": v(133.96, -45) * mm, "construction": true});
            skLineSegment(sketch, "E12", {"start": v(88.96, 0) * mm, "end": v(178.96, 0) * mm, "construction": true});
            skLineSegment(sketch, "E13.MirrorCS", {"start": v(123.96, 0) * mm, "end": v(123.96, 5) * mm});
            skLineSegment(sketch, "E14.MirrorCS", {"start": v(128.96, 0) * mm, "end": v(128.96, 5) * mm});
            skLineSegment(sketch, "E15.MirrorCS", {"start": v(143.96, 0) * mm, "end": v(143.96, -5) * mm});
            skLineSegment(sketch, "E16.MirrorCS", {"start": v(138.96, 0) * mm, "end": v(138.96, -5) * mm});
            skLineSegment(sketch, "E17.MirrorCS", {"start": v(123.96, 0) * mm, "end": v(123.96, -5) * mm});
            skLineSegment(sketch, "E18.MirrorCS", {"start": v(128.96, 0) * mm, "end": v(128.96, -5) * mm});
            skLineSegment(sketch, "E19.0", {"start": v(89.24, -5) * mm, "end": v(123.96, -5) * mm});
            skLineSegment(sketch, "E20.0", {"start": v(90.08, -10) * mm, "end": v(123.96, -10) * mm});
            skLineSegment(sketch, "E21.MirrorCS", {"start": v(89.24, 5) * mm, "end": v(123.96, 5) * mm});
            skLineSegment(sketch, "E22.MirrorCS", {"start": v(90.08, 10) * mm, "end": v(123.96, 10) * mm});
            skLineSegment(sketch, "E23.trimOffspring", {"start": v(123.96, 10) * mm, "end": v(123.96, 43.87) * mm});
            skLineSegment(sketch, "E24.trimOffspring", {"start": v(128.96, 10) * mm, "end": v(138.96, 10) * mm});
            skLineSegment(sketch, "E25.trimOffspring", {"start": v(128.96, 10) * mm, "end": v(128.96, 44.72) * mm});
            skLineSegment(sketch, "E26.trimOffspring", {"start": v(128.96, 5) * mm, "end": v(138.96, 5) * mm});
            skLineSegment(sketch, "E27.trimOffspring", {"start": v(128.96, -5) * mm, "end": v(138.96, -5) * mm});
            skLineSegment(sketch, "E28.trimOffspring", {"start": v(123.96, -10) * mm, "end": v(123.96, -43.87) * mm});
            skLineSegment(sketch, "E29.trimOffspring", {"start": v(128.96, -10) * mm, "end": v(128.96, -44.72) * mm});
            skLineSegment(sketch, "E30.trimOffspring", {"start": v(128.96, -10) * mm, "end": v(138.96, -10) * mm});
            skLineSegment(sketch, "E31.trimOffspring", {"start": v(138.96, -10) * mm, "end": v(138.96, -44.72) * mm});
            skLineSegment(sketch, "E32.trimOffspring", {"start": v(143.96, -10) * mm, "end": v(177.83, -10) * mm});
            skLineSegment(sketch, "E33.trimOffspring", {"start": v(143.96, -5) * mm, "end": v(178.68, -5) * mm});
            skLineSegment(sketch, "E34.trimOffspring", {"start": v(143.96, -10) * mm, "end": v(143.96, -43.87) * mm});
            skLineSegment(sketch, "E35.trimOffspring", {"start": v(143.96, 5) * mm, "end": v(178.68, 5) * mm});
            skLineSegment(sketch, "E36.trimOffspring", {"start": v(143.96, 10) * mm, "end": v(143.96, 43.87) * mm});
            skLineSegment(sketch, "E37.trimOffspring", {"start": v(143.96, 10) * mm, "end": v(177.83, 10) * mm});
            skLineSegment(sketch, "E38.trimOffspring", {"start": v(138.96, 10) * mm, "end": v(138.96, 44.72) * mm});
            skLineSegment(sketch, "E39", {"start": v(143.96, 10) * mm, "end": v(171.22, 25.23) * mm});
            skLineSegment(sketch, "E40.0", {"start": v(150.1, 10) * mm, "end": v(172.82, 22.7) * mm});
            skLineSegment(sketch, "E41", {"start": v(133.96, 0) * mm, "end": v(143.96, 10) * mm, "construction": true});
            skLineSegment(sketch, "E42", {"start": v(123.96, 10) * mm, "end": v(143.96, -10) * mm, "construction": true});
            skLineSegment(sketch, "E43.MirrorCS", {"start": v(143.96, 10) * mm, "end": v(159.2, 37.26) * mm});
            skLineSegment(sketch, "E44.MirrorCS", {"start": v(123.96, 10) * mm, "end": v(96.7, 25.23) * mm});
            skLineSegment(sketch, "E45.MirrorCS", {"start": v(123.96, 10) * mm, "end": v(108.73, 37.26) * mm});
            skLineSegment(sketch, "E46.MirrorCS", {"start": v(143.96, -10) * mm, "end": v(171.22, -25.23) * mm});
            skLineSegment(sketch, "E47.MirrorCS", {"start": v(143.96, -10) * mm, "end": v(159.2, -37.26) * mm});
            skLineSegment(sketch, "E48.MirrorCS", {"start": v(123.96, -10) * mm, "end": v(108.73, -37.26) * mm});
            skLineSegment(sketch, "E49.MirrorCS", {"start": v(123.96, -10) * mm, "end": v(96.7, -25.23) * mm});
            skPoint(sketch, "E50.orphan", {"position": v(170.96, 21.65) * mm});
            skLineSegment(sketch, "E51.MirrorCS", {"start": v(143.96, 16.15) * mm, "end": v(156.65, 38.86) * mm});
            skLineSegment(sketch, "E52.MirrorCS", {"start": v(123.96, 16.15) * mm, "end": v(111.27, 38.86) * mm});
            skLineSegment(sketch, "E53.MirrorCS", {"start": v(117.8, 10) * mm, "end": v(95.1, 22.7) * mm});
            skLineSegment(sketch, "E54.MirrorCS", {"start": v(117.8, -10) * mm, "end": v(95.1, -22.7) * mm});
            skLineSegment(sketch, "E55.MirrorCS", {"start": v(123.96, -16.15) * mm, "end": v(111.27, -38.86) * mm});
            skLineSegment(sketch, "E56.MirrorCS", {"start": v(143.96, -16.15) * mm, "end": v(156.65, -38.86) * mm});
            skLineSegment(sketch, "E57.MirrorCS", {"start": v(150.1, -10) * mm, "end": v(172.82, -22.7) * mm});
            skLineSegment(sketch, "E58.bottom", {"start": v(261.43, -4.75) * mm, "end": v(251.93, -4.75) * mm});
            skLineSegment(sketch, "E58.top", {"start": v(261.43, 4.75) * mm, "end": v(251.93, 4.75) * mm});
            skLineSegment(sketch, "E58.left", {"start": v(261.43, -4.75) * mm, "end": v(261.43, 4.75) * mm});
            skLineSegment(sketch, "E58.right", {"start": v(251.93, -4.75) * mm, "end": v(251.93, 4.75) * mm});
            skPoint(sketch, "E58.middle", {"position": v(256.68, 0) * mm});
            skCircle(sketch, "E59", {"center": v(256.68, 0) * mm, "radius": 0.5 * mm});
            skSolve(sketch);
        }
        {
            var Q0;
            Q0=makeQuery(id+"F5.imprint","IMPRINT",FACE,{"disambiguationData":[TD([[makeQuery(id+"F5.imprint","IMPRINT",EDGE,{"derivedFrom":sQuery(id+"F5.wireOp",EDGE,"E9")}),-1.0]])]});
            extrude(context, id + "F6", {"entities" : qUnion([Q0]), "depth" : 3 * mm});
        }
        {
            var Q0;
            {var subQ0=sQuery(id+"F5.wireOp",EDGE,"E44.MirrorCS");Q0=makeQuery(id+"F5.imprint","IMPRINT",FACE,{"disambiguationData":[TD([[makeQuery(id+"F5.imprint","IMPRINT",EDGE,{"derivedFrom":subQ0}),1.0]])]});}
            var Q1;
            {var subQ0=sQuery(id+"F5.wireOp",EDGE,"E45.MirrorCS");Q1=makeQuery(id+"F5.imprint","IMPRINT",FACE,{"disambiguationData":[TD([[makeQuery(id+"F5.imprint","IMPRINT",EDGE,{"derivedFrom":subQ0}),-1.0]])]});}
            var Q2;
            {var subQ0=sQuery(id+"F5.wireOp",EDGE,"E43.MirrorCS");Q2=makeQuery(id+"F5.imprint","IMPRINT",FACE,{"disambiguationData":[TD([[makeQuery(id+"F5.imprint","IMPRINT",EDGE,{"derivedFrom":subQ0}),1.0]])]});}
            var Q3;
            {var subQ0=sQuery(id+"F5.wireOp",EDGE,"E39");Q3=makeQuery(id+"F5.imprint","IMPRINT",FACE,{"disambiguationData":[TD([[makeQuery(id+"F5.imprint","IMPRINT",EDGE,{"derivedFrom":subQ0}),-1.0]])]});}
            var Q4;
            {var subQ0=sQuery(id+"F5.wireOp",EDGE,"E46.MirrorCS");Q4=makeQuery(id+"F5.imprint","IMPRINT",FACE,{"disambiguationData":[TD([[makeQuery(id+"F5.imprint","IMPRINT",EDGE,{"derivedFrom":subQ0}),1.0]])]});}
            var Q5;
            {var subQ0=sQuery(id+"F5.wireOp",EDGE,"E47.MirrorCS");Q5=makeQuery(id+"F5.imprint","IMPRINT",FACE,{"disambiguationData":[TD([[makeQuery(id+"F5.imprint","IMPRINT",EDGE,{"derivedFrom":subQ0}),-1.0]])]});}
            var Q6;
            {var subQ0=sQuery(id+"F5.wireOp",EDGE,"E48.MirrorCS");Q6=makeQuery(id+"F5.imprint","IMPRINT",FACE,{"disambiguationData":[TD([[makeQuery(id+"F5.imprint","IMPRINT",EDGE,{"derivedFrom":subQ0}),1.0]])]});}
            var Q7;
            {var subQ0=sQuery(id+"F5.wireOp",EDGE,"E49.MirrorCS");Q7=makeQuery(id+"F5.imprint","IMPRINT",FACE,{"disambiguationData":[TD([[makeQuery(id+"F5.imprint","IMPRINT",EDGE,{"derivedFrom":subQ0}),-1.0]])]});}
            extrude(context, id + "F7", {"entities" : qUnion([Q0, Q1, Q2, Q3, Q4, Q5, Q6, Q7]), "operationType" : NewBodyOperationType.ADD, "depth" : 2 * mm});
        }
        {
            var Q0;
            Q0=makeQuery(id+"F5.imprint","IMPRINT",FACE,{"disambiguationData":[TD([[makeQuery(id+"F5.imprint","IMPRINT",EDGE,{"derivedFrom":sQuery(id+"F5.wireOp",EDGE,"E58.bottom")}),-1.0]])]});
            var Q1;
            Q1=makeQuery(id+"F5.imprint","IMPRINT",FACE,{"disambiguationData":[TD([[makeQuery(id+"F5.imprint","IMPRINT",EDGE,{"derivedFrom":sQuery(id+"F5.wireOp",EDGE,"E59")}),1.0]])]});
            extrude(context, id + "F8", {"entities" : qUnion([Q0, Q1]), "depth" : 50 * mm});
        }
        {
            var Q0;
            Q0=makeQuery(id+"F5.imprint","IMPRINT",FACE,{"disambiguationData":[TD([[makeQuery(id+"F5.imprint","IMPRINT",EDGE,{"derivedFrom":sQuery(id+"F5.wireOp",EDGE,"E59")}),1.0]])]});
            extrude(context, id + "F9", {"entities" : qUnion([Q0]), "operationType" : NewBodyOperationType.REMOVE, "depth" : 2 * mm});
        }
        {
            var Q0;
            Q0=makeQuery(id+"F8.opExtrude","SWEPT_BODY",BODY,{"disambiguationData":[OSD([sQuery(id+"F5.wireOp",EDGE,"E58.bottom"),sQuery(id+"F5.wireOp",EDGE,"E58.top"),sQuery(id+"F5.wireOp",EDGE,"E58.left"),sQuery(id+"F5.wireOp",EDGE,"E58.right")])]});
            var Q1;
            Q1=makeQuery(id+"F8.opExtrude","CAP_FACE",FACE,{"disambiguationData":[OSD([sQuery(id+"F5.wireOp",EDGE,"E58.bottom"),sQuery(id+"F5.wireOp",EDGE,"E58.top"),sQuery(id+"F5.wireOp",EDGE,"E58.left"),sQuery(id+"F5.wireOp",EDGE,"E58.right")])],"isStart":false});
            mirror(context, id + "F10", {"operationType" : NewBodyOperationType.ADD, "entities" : qUnion([Q0]), "mirrorPlane" : qUnion([Q1])});
        }
    });
